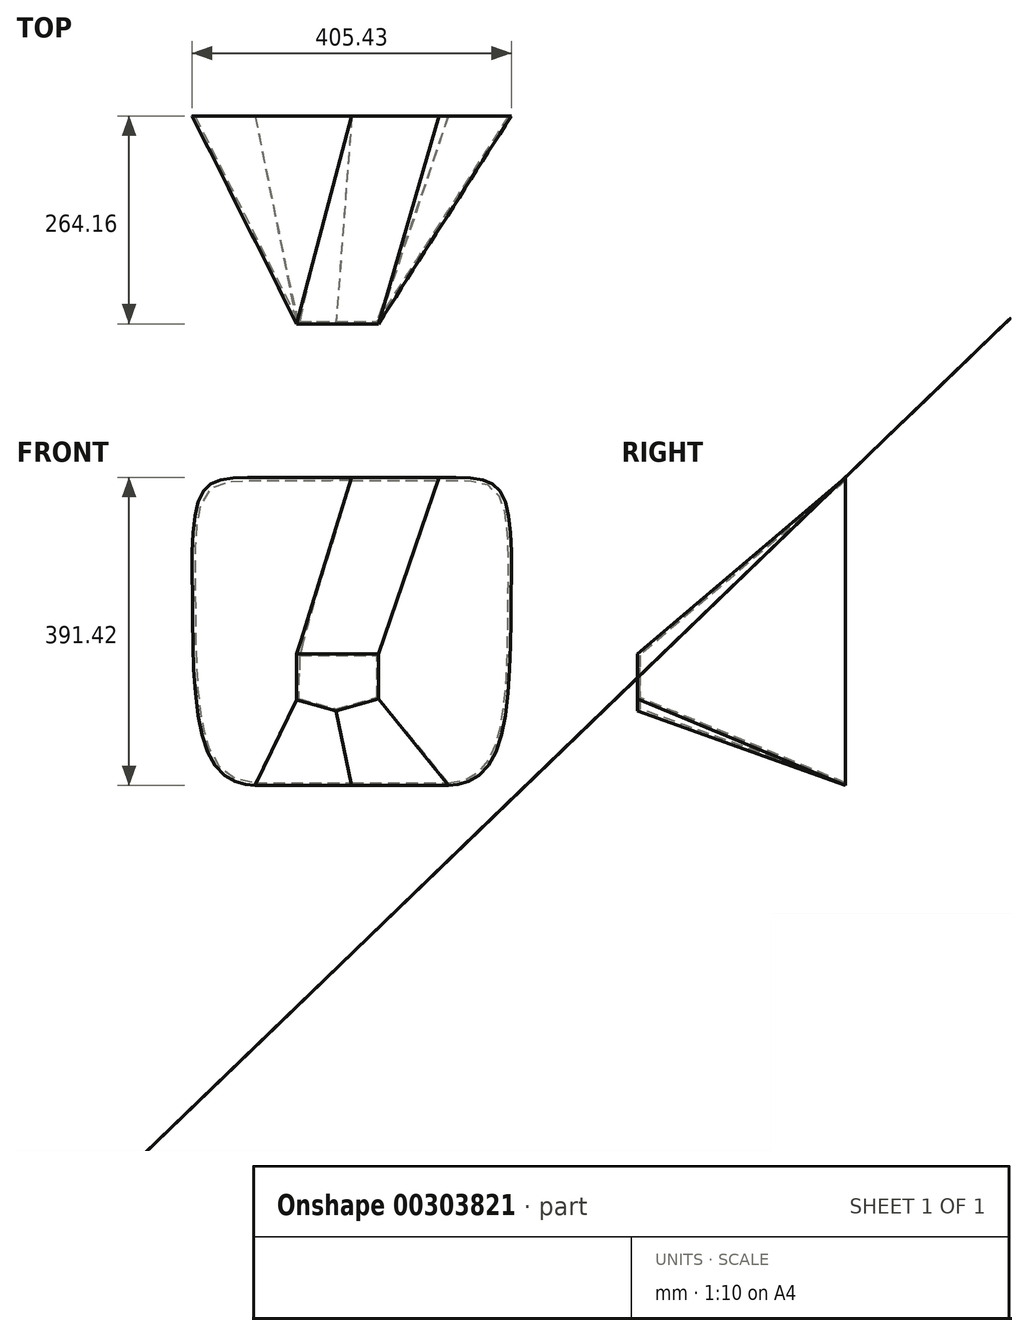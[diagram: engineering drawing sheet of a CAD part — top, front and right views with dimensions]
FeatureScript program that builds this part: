
annotation { "Feature Type Name" : "Feature", "Feature Type Description" : "" }
export const myFeature = defineFeature(function(context is Context, id is Id, definition is map)
    precondition{}
    {
        {
            var Q0;
            Q0=qCreatedBy(makeId("Front.planeOp"),FACE);
            var sketch = newSketch(context, id + "F0", { "sketchPlane" : qUnion([Q0])});
            skLineSegment(sketch, "E0", {"start": v(-1.5, -316.33) * mm, "end": v(-1.5, 733.8) * mm, "construction": true});
            skLineSegment(sketch, "E1", {"start": v(121.35, -155.37) * mm, "end": v(-1.5, -155.37) * mm});
            skLineSegment(sketch, "E2.MirrorCS", {"start": v(-124.36, -155.37) * mm, "end": v(-1.5, -155.37) * mm});
            skPoint(sketch, "E3.end.orphan", {"position": v(109.4, 236.05) * mm});
            skPoint(sketch, "E3.start.orphan", {"position": v(-1.5, 236.05) * mm});
            skLineSegment(sketch, "E4", {"start": v(-1.5, 236.05) * mm, "end": v(109.4, 236.05) * mm});
            skFitSpline(sketch, "E5", {"points": [v(109.4, 236.05) * mm, v(184.46, 222.14) * mm, v(200.9, 84.03) * mm, v(173.46, -128.34) * mm, v(121.35, -155.37) * mm], "startDerivative": vector(532.35, -8.33) * mm, "endDerivative": vector(-257.37, 0) * mm});
            skPoint(sketch, "E6.MirrorCS.end.orphan", {"position": v(-112.41, 236.05) * mm});
            skPoint(sketch, "E7.MirrorCS.end.orphan", {"position": v(-124.36, -155.37) * mm});
            skLineSegment(sketch, "E8.MirrorCS", {"start": v(-1.5, 236.05) * mm, "end": v(-112.41, 236.05) * mm});
            skFitSpline(sketch, "E9.MirrorCS", {"points": [v(-112.41, 236.05) * mm, v(-187.48, 222.14) * mm, v(-203.9, 84.03) * mm, v(-176.47, -128.34) * mm, v(-124.36, -155.37) * mm], "startDerivative": vector(-532.35, -8.33) * mm, "endDerivative": vector(257.37, 0) * mm});
            skSolve(sketch);
        }
        {
            var Q0;
            Q0=qCreatedBy(makeId("Front.planeOp"),FACE);
            cPlane(context, id + "F1", {"entities" : qUnion([Q0]), "cplaneType" : CPlaneType.OFFSET, "offset" : 142.24 * mm, "width" : 152.4 * mm, "height" : 152.4 * mm});
        }
        {
            var Q0;
            Q0=qCreatedBy(makeId("Front.planeOp"),FACE);
            cPlane(context, id + "F2", {"entities" : qUnion([Q0]), "cplaneType" : CPlaneType.OFFSET, "offset" : 220.98 * mm, "width" : 152.4 * mm, "height" : 152.4 * mm});
        }
        {
            var Q0;
            Q0=qCreatedBy(makeId("Front.planeOp"),FACE);
            cPlane(context, id + "F3", {"entities" : qUnion([Q0]), "cplaneType" : CPlaneType.OFFSET, "offset" : 264.16 * mm, "width" : 152.4 * mm, "height" : 152.4 * mm});
        }
        {
            var Q0;
            Q0=qCreatedBy(id+"F3.planeOp",FACE);
            var sketch = newSketch(context, id + "F4", { "sketchPlane" : qUnion([Q0])});
            skLineSegment(sketch, "E10", {"start": v(-71.37, 11.58) * mm, "end": v(32.39, 11.58) * mm});
            skLineSegment(sketch, "E11", {"start": v(32.39, 11.58) * mm, "end": v(32.39, -45.14) * mm});
            skLineSegment(sketch, "E12", {"start": v(32.39, -45.14) * mm, "end": v(-21.57, -60.36) * mm});
            skLineSegment(sketch, "E13", {"start": v(-21.57, -60.36) * mm, "end": v(-71.37, -46.52) * mm});
            skLineSegment(sketch, "E14", {"start": v(-71.37, -46.52) * mm, "end": v(-71.37, -18.85) * mm});
            skLineSegment(sketch, "E15", {"start": v(-71.37, -18.85) * mm, "end": v(-71.37, 11.58) * mm});
            skSolve(sketch);
        }
        {
            var Q0;
            Q0=makeQuery(id+"F0.imprint","IMPRINT",FACE,{"disambiguationData":[TD([[makeQuery(id+"F0.imprint","IMPRINT",EDGE,{"derivedFrom":sQuery(id+"F0.wireOp",EDGE,"E2.MirrorCS")}),1.0]])]});
            var Q1;
            Q1=makeQuery(id+"F4.imprint","IMPRINT",FACE,{"disambiguationData":[TD([[makeQuery(id+"F4.imprint","IMPRINT",EDGE,{"derivedFrom":sQuery(id+"F4.wireOp",EDGE,"E10")}),-1.0]])]});
            loft(context, id + "F5", {"sheetProfilesArray" : [{ "sheetProfileEntities" : qUnion([Q0]) }, { "sheetProfileEntities" : qUnion([Q1]) }]});
        }
        {
            var Q0;
            Q0=makeQuery(id+"F5.opLoft","CAP_FACE",FACE,{"disambiguationData":[OSD([makeQuery(id+"F0.imprint","IMPRINT",FACE,{"disambiguationData":[TD([[makeQuery(id+"F0.imprint","IMPRINT",EDGE,{"derivedFrom":sQuery(id+"F0.wireOp",EDGE,"E2.MirrorCS")}),1.0]])]})])],"isStart":true});
            shell(context, id + "F6", {"entities" : qUnion([Q0]), "thickness" : 3.17 * mm});
        }
    });
